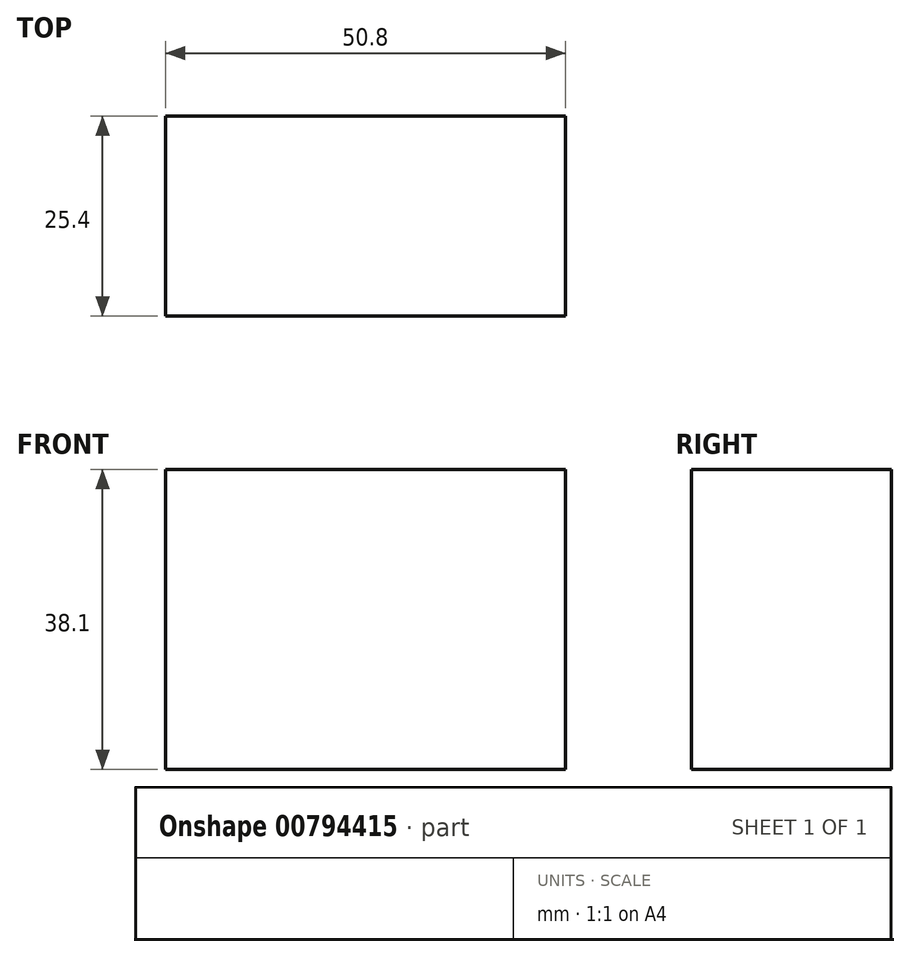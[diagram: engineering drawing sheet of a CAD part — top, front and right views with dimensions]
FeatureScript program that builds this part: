
annotation { "Feature Type Name" : "Feature", "Feature Type Description" : "" }
export const myFeature = defineFeature(function(context is Context, id is Id, definition is map)
    precondition{}
    {
        {
            var Q0;
            Q0=qCreatedBy(makeId("Right.planeOp"),FACE);
            var sketch = newSketch(context, id + "F0", { "sketchPlane" : qUnion([Q0])});
            skLineSegment(sketch, "E0", {"start": v(0, 0) * mm, "end": v(25.4, 0) * mm});
            skLineSegment(sketch, "E1", {"start": v(25.4, 0) * mm, "end": v(25.4, 38.1) * mm});
            skLineSegment(sketch, "E2", {"start": v(25.4, 38.1) * mm, "end": v(0, 38.1) * mm});
            skLineSegment(sketch, "E3", {"start": v(0, 38.1) * mm, "end": v(0, 0) * mm});
            skSolve(sketch);
        }
        {
            var Q0;
            Q0 = qSketchRegion(id + "F0", true);
            extrude(context, id + "F1", {"entities" : qUnion([Q0]), "depth" : 50.8 * mm, "offsetDistance" : 25.4 * mm});
        }
    });
